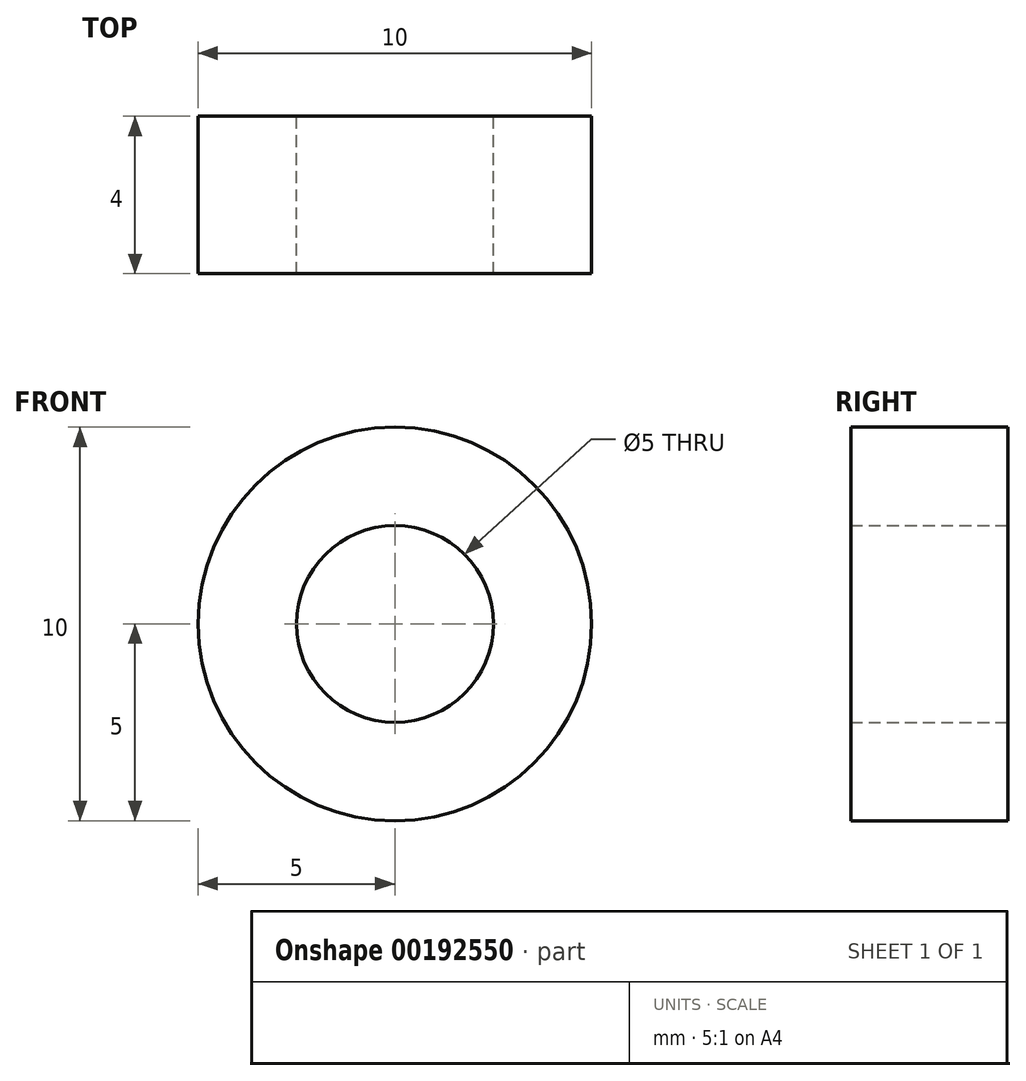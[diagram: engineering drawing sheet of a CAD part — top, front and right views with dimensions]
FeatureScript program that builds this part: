
annotation { "Feature Type Name" : "Feature", "Feature Type Description" : "" }
export const myFeature = defineFeature(function(context is Context, id is Id, definition is map)
    precondition{}
    {
        {
            var Q0;
            Q0=qCreatedBy(makeId("Front.planeOp"),FACE);
            var sketch = newSketch(context, id + "F0", { "sketchPlane" : qUnion([Q0])});
            skCircle(sketch, "E0", {"center": v(0, 0) * mm, "radius": 5 * mm});
            skSolve(sketch);
        }
        {
            var Q0;
            Q0 = qSketchRegion(id + "F0", true);
            extrude(context, id + "F1", {"entities" : qUnion([Q0]), "depth" : 4 * mm});
        }
        {
            var Q0;
            Q0=qCreatedBy(makeId("Front.planeOp"),FACE);
            var sketch = newSketch(context, id + "F2", { "sketchPlane" : qUnion([Q0])});
            skCircle(sketch, "E1", {"center": v(0, 0) * mm, "radius": 2.5 * mm});
            skSolve(sketch);
        }
        {
            var Q0;
            Q0 = qSketchRegion(id + "F2", true);
            extrude(context, id + "F3", {"entities" : qUnion([Q0]), "operationType" : NewBodyOperationType.REMOVE, "endBound" : BoundingType.UP_TO_NEXT, "depth" : 25 * mm});
        }
    });
